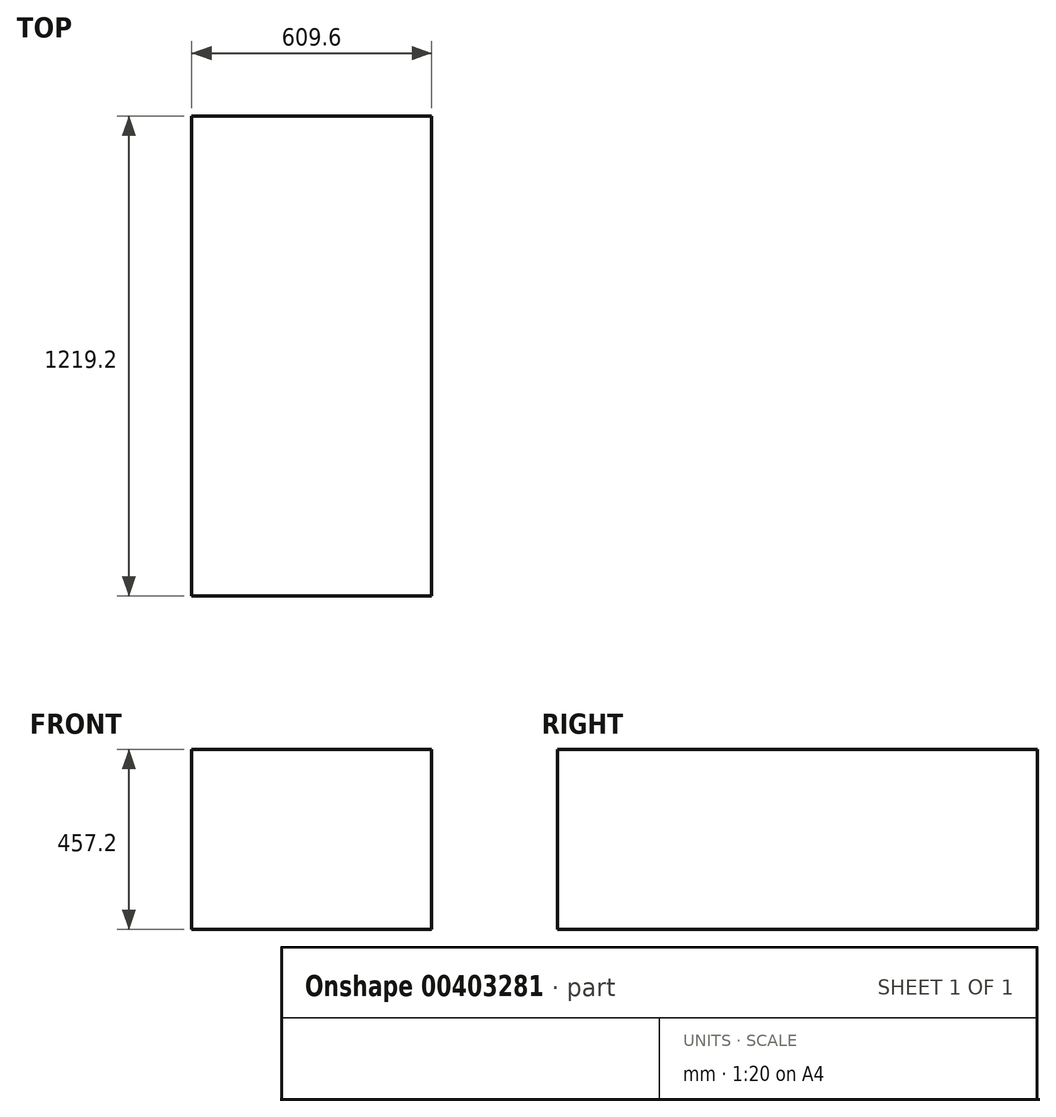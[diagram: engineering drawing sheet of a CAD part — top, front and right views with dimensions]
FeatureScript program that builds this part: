
annotation { "Feature Type Name" : "Feature", "Feature Type Description" : "" }
export const myFeature = defineFeature(function(context is Context, id is Id, definition is map)
    precondition{}
    {
        {
            var Q0;
            Q0=qCreatedBy(makeId("Front.planeOp"),FACE);
            var sketch = newSketch(context, id + "F0", { "sketchPlane" : qUnion([Q0])});
            skLineSegment(sketch, "E0.bottom", {"start": v(0, 0) * mm, "end": v(-609.6, 0) * mm});
            skLineSegment(sketch, "E0.top", {"start": v(0, 457.2) * mm, "end": v(-609.6, 457.2) * mm});
            skLineSegment(sketch, "E0.left", {"start": v(0, 0) * mm, "end": v(0, 457.2) * mm});
            skLineSegment(sketch, "E0.right", {"start": v(-609.6, 0) * mm, "end": v(-609.6, 457.2) * mm});
            skSolve(sketch);
        }
        {
            var Q0;
            Q0 = qSketchRegion(id + "F0", true);
            extrude(context, id + "F1", {"entities" : qUnion([Q0]), "depth" : 1219.2 * mm});
        }
    });
